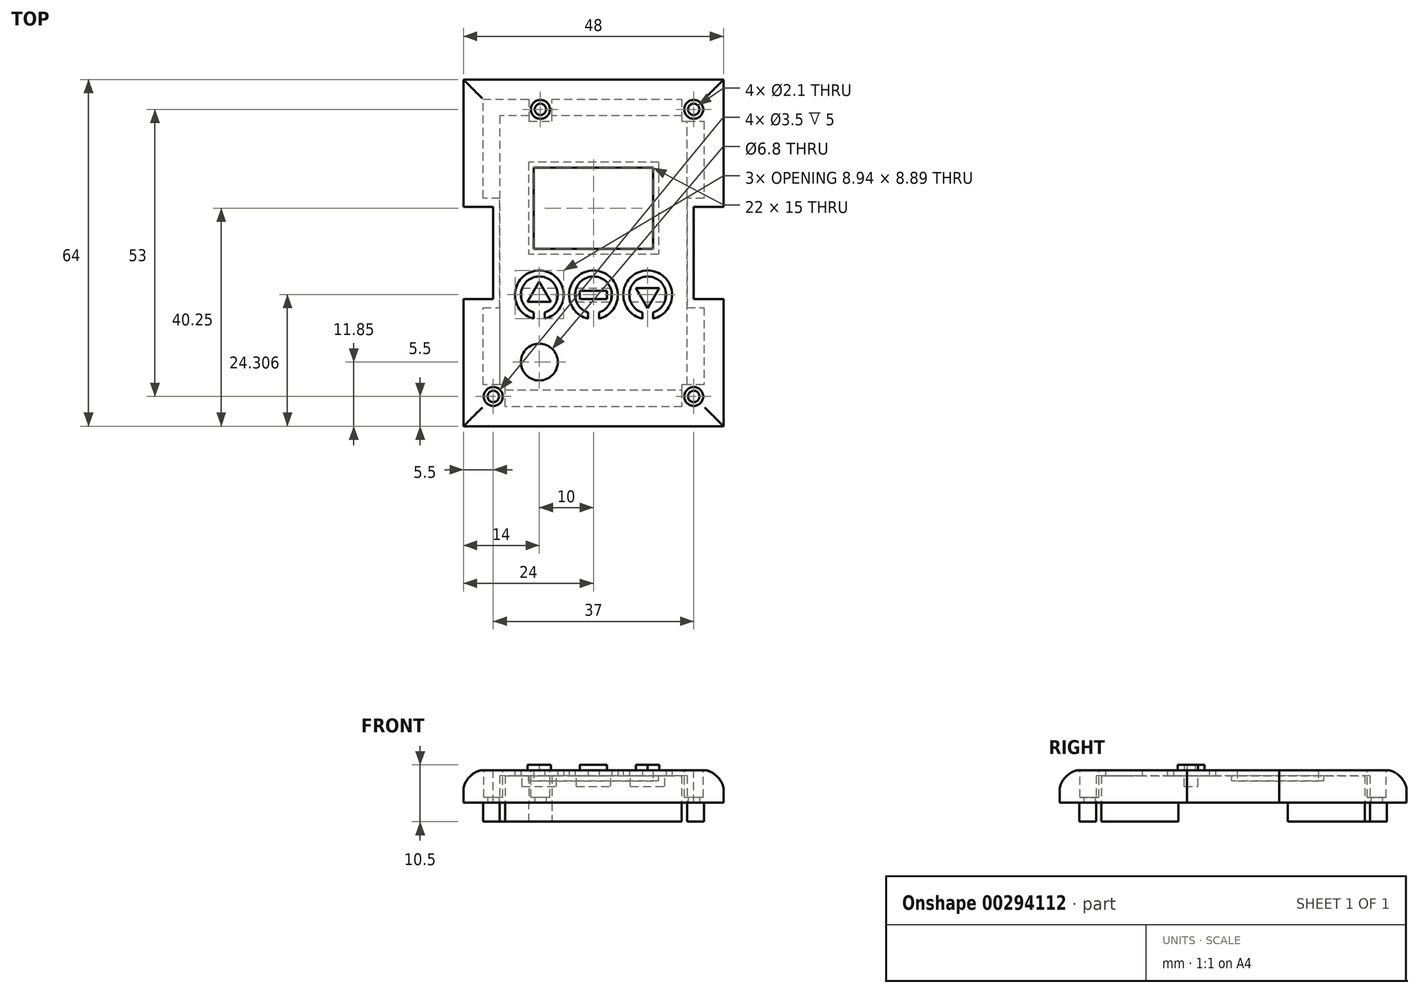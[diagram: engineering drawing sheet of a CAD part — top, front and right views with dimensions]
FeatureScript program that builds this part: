
annotation { "Feature Type Name" : "Feature", "Feature Type Description" : "" }
export const myFeature = defineFeature(function(context is Context, id is Id, definition is map)
    precondition{}
    {
        {
            var Q0;
            Q0=qCreatedBy(makeId("Top.planeOp"),FACE);
            var sketch = newSketch(context, id + "F0", { "sketchPlane" : qUnion([Q0])});
            skLineSegment(sketch, "E0.bottom", {"start": v(24, 32) * mm, "end": v(-24, 32) * mm});
            skLineSegment(sketch, "E0.top", {"start": v(24, -32) * mm, "end": v(-24, -32) * mm});
            skLineSegment(sketch, "E0.left", {"start": v(24, 32) * mm, "end": v(24, -32) * mm});
            skLineSegment(sketch, "E0.right", {"start": v(-24, 32) * mm, "end": v(-24, -32) * mm});
            skPoint(sketch, "E0.middle", {"position": v(0, 0) * mm});
            skSolve(sketch);
        }
        {
            var Q0;
            Q0=qSketchRegion(id+"F0",true);
            extrude(context, id + "F1", {"entities" : qUnion([Q0]), "depth" : 6 * mm});
        }
        {
            var Q0;
            Q0=makeQuery(id+"F1.opExtrude","CAP_FACE",FACE,{"disambiguationData":[OSD([sQuery(id+"F0.wireOp",EDGE,"E0.bottom"),sQuery(id+"F0.wireOp",EDGE,"E0.top"),sQuery(id+"F0.wireOp",EDGE,"E0.left"),sQuery(id+"F0.wireOp",EDGE,"E0.right")])],"isStart":false});
            var sketch = newSketch(context, id + "F2", { "sketchPlane" : qUnion([Q0])});
            skLineSegment(sketch, "E1.bottom", {"start": v(-24, 8.5) * mm, "end": v(-18.5, 8.5) * mm});
            skLineSegment(sketch, "E1.top", {"start": v(-24, -8.5) * mm, "end": v(-18.5, -8.5) * mm});
            skLineSegment(sketch, "E1.left", {"start": v(-24, 8.5) * mm, "end": v(-24, -8.5) * mm});
            skLineSegment(sketch, "E1.right", {"start": v(-18.5, 8.5) * mm, "end": v(-18.5, -8.5) * mm});
            skPoint(sketch, "E1.middle", {"position": v(-21.25, 0) * mm});
            skLineSegment(sketch, "E2.bottom", {"start": v(24, 8.5) * mm, "end": v(18.5, 8.5) * mm});
            skLineSegment(sketch, "E2.top", {"start": v(24, -8.5) * mm, "end": v(18.5, -8.5) * mm});
            skLineSegment(sketch, "E2.left", {"start": v(24, 8.5) * mm, "end": v(24, -8.5) * mm});
            skLineSegment(sketch, "E2.right", {"start": v(18.5, 8.5) * mm, "end": v(18.5, -8.5) * mm});
            skPoint(sketch, "E2.middle", {"position": v(21.25, 0) * mm});
            skSolve(sketch);
        }
        {
            var Q0;
            Q0=qSketchRegion(id+"F2",true);
            extrude(context, id + "F3", {"entities" : qUnion([Q0]), "operationType" : NewBodyOperationType.REMOVE, "endBound" : BoundingType.THROUGH_ALL, "oppositeDirection" : true, "depth" : 25 * mm});
        }
        {
            var Q0;
            Q0=makeQuery(id+"F1.opExtrude","CAP_FACE",FACE,{"disambiguationData":[OSD([sQuery(id+"F0.wireOp",EDGE,"E0.bottom"),sQuery(id+"F0.wireOp",EDGE,"E0.top"),sQuery(id+"F0.wireOp",EDGE,"E0.left"),sQuery(id+"F0.wireOp",EDGE,"E0.right")])],"isStart":true});
            var sketch = newSketch(context, id + "F4", { "sketchPlane" : qUnion([Q0])});
            skLineSegment(sketch, "E3", {"start": v(-20.4, -28.4) * mm, "end": v(-11.9, -28.4) * mm});
            skLineSegment(sketch, "E4", {"start": v(-11.9, -28.4) * mm, "end": v(-11.9, -24.3) * mm});
            skLineSegment(sketch, "E5", {"start": v(-11.9, -24.3) * mm, "end": v(-7.7, -24.3) * mm});
            skLineSegment(sketch, "E6", {"start": v(-7.7, -24.3) * mm, "end": v(-7.7, -28.4) * mm});
            skLineSegment(sketch, "E7", {"start": v(-7.7, -28.4) * mm, "end": v(16.3, -28.4) * mm});
            skLineSegment(sketch, "E8", {"start": v(16.3, -28.4) * mm, "end": v(16.3, -24.3) * mm});
            skLineSegment(sketch, "E9", {"start": v(16.3, -24.3) * mm, "end": v(20.4, -24.3) * mm});
            skLineSegment(sketch, "E10", {"start": v(20.4, -24.3) * mm, "end": v(20.4, -10.1) * mm});
            skLineSegment(sketch, "E11", {"start": v(20.4, -10.1) * mm, "end": v(15.5, -10.1) * mm});
            skLineSegment(sketch, "E12", {"start": v(15.5, -10.1) * mm, "end": v(15.5, 10.1) * mm});
            skLineSegment(sketch, "E13", {"start": v(15.5, 10.1) * mm, "end": v(20.4, 10.1) * mm});
            skLineSegment(sketch, "E14", {"start": v(20.4, 10.1) * mm, "end": v(20.4, 24.3) * mm});
            skLineSegment(sketch, "E15", {"start": v(20.4, 24.3) * mm, "end": v(16.3, 24.3) * mm});
            skLineSegment(sketch, "E16", {"start": v(16.3, 24.3) * mm, "end": v(16.3, 28.4) * mm});
            skLineSegment(sketch, "E17", {"start": v(16.3, 28.4) * mm, "end": v(-16.3, 28.4) * mm});
            skLineSegment(sketch, "E18", {"start": v(-16.3, 28.4) * mm, "end": v(-16.3, 24.3) * mm});
            skLineSegment(sketch, "E19", {"start": v(-16.3, 24.3) * mm, "end": v(-20.4, 24.3) * mm});
            skLineSegment(sketch, "E20", {"start": v(-20.4, 24.3) * mm, "end": v(-20.4, 10.1) * mm});
            skLineSegment(sketch, "E21", {"start": v(-20.4, 10.1) * mm, "end": v(-15.5, 10.1) * mm});
            skLineSegment(sketch, "E22", {"start": v(-15.5, 10.1) * mm, "end": v(-15.5, -10.1) * mm});
            skLineSegment(sketch, "E23", {"start": v(-15.5, -10.1) * mm, "end": v(-20.4, -10.1) * mm});
            skLineSegment(sketch, "E24", {"start": v(-20.4, -10.1) * mm, "end": v(-20.4, -28.4) * mm});
            skSolve(sketch);
        }
        {
            var Q0;
            Q0=qSketchRegion(id+"F4",true);
            extrude(context, id + "F5", {"entities" : qUnion([Q0]), "operationType" : NewBodyOperationType.ADD, "depth" : 3.5 * mm});
        }
        {
            var Q0;
            Q0=makeQuery(id+"F5.opExtrude","CAP_FACE",FACE,{"disambiguationData":[OSD([sQuery(id+"F4.wireOp",EDGE,"E3"),sQuery(id+"F4.wireOp",EDGE,"E4"),sQuery(id+"F4.wireOp",EDGE,"E5"),sQuery(id+"F4.wireOp",EDGE,"E6"),sQuery(id+"F4.wireOp",EDGE,"E7"),sQuery(id+"F4.wireOp",EDGE,"E8"),sQuery(id+"F4.wireOp",EDGE,"E9"),sQuery(id+"F4.wireOp",EDGE,"E10"),sQuery(id+"F4.wireOp",EDGE,"E11"),sQuery(id+"F4.wireOp",EDGE,"E12"),sQuery(id+"F4.wireOp",EDGE,"E13"),sQuery(id+"F4.wireOp",EDGE,"E14"),sQuery(id+"F4.wireOp",EDGE,"E15"),sQuery(id+"F4.wireOp",EDGE,"E16"),sQuery(id+"F4.wireOp",EDGE,"E17"),sQuery(id+"F4.wireOp",EDGE,"E18"),sQuery(id+"F4.wireOp",EDGE,"E19"),sQuery(id+"F4.wireOp",EDGE,"E20"),sQuery(id+"F4.wireOp",EDGE,"E21"),sQuery(id+"F4.wireOp",EDGE,"E22"),sQuery(id+"F4.wireOp",EDGE,"E23"),sQuery(id+"F4.wireOp",EDGE,"E24")])],"isStart":false});
            var sketch = newSketch(context, id + "F6", { "sketchPlane" : qUnion([Q0])});
            skLineSegment(sketch, "E25", {"start": v(-16.3, 24.3) * mm, "end": v(-16.3, 25.3) * mm});
            skLineSegment(sketch, "E26", {"start": v(-16.3, 25.3) * mm, "end": v(16.3, 25.3) * mm});
            skLineSegment(sketch, "E27", {"start": v(16.3, 25.3) * mm, "end": v(16.3, 24.3) * mm});
            skLineSegment(sketch, "E28", {"start": v(16.3, 24.3) * mm, "end": v(17.3, 24.3) * mm});
            skPoint(sketch, "E29.endSnap0", {"position": v(17.95, 10.1) * mm});
            skLineSegment(sketch, "E30", {"start": v(17.3, 24.3) * mm, "end": v(17.3, -24.3) * mm});
            skLineSegment(sketch, "E31", {"start": v(17.3, -24.3) * mm, "end": v(16.3, -24.3) * mm});
            skLineSegment(sketch, "E32", {"start": v(16.3, -24.3) * mm, "end": v(16.3, -25.3) * mm});
            skLineSegment(sketch, "E33", {"start": v(16.3, -25.3) * mm, "end": v(-7.7, -25.3) * mm});
            skLineSegment(sketch, "E34", {"start": v(-7.7, -25.3) * mm, "end": v(-7.7, -24.3) * mm});
            skLineSegment(sketch, "E35", {"start": v(-7.7, -24.3) * mm, "end": v(-11.9, -24.3) * mm});
            skLineSegment(sketch, "E36", {"start": v(-11.9, -24.3) * mm, "end": v(-11.9, -25.3) * mm});
            skLineSegment(sketch, "E37", {"start": v(-11.9, -25.3) * mm, "end": v(-17.3, -25.3) * mm});
            skLineSegment(sketch, "E38", {"start": v(-17.3, -25.3) * mm, "end": v(-17.3, 24.3) * mm});
            skLineSegment(sketch, "E39", {"start": v(-17.3, 24.3) * mm, "end": v(-16.3, 24.3) * mm});
            skSolve(sketch);
        }
        {
            var Q0;
            Q0=qSketchRegion(id+"F6",true);
            extrude(context, id + "F7", {"entities" : qUnion([Q0]), "operationType" : NewBodyOperationType.REMOVE, "oppositeDirection" : true, "depth" : 8.5 * mm});
        }
        {
            var Q0;
            Q0=makeQuery(id+"F1.opExtrude","CAP_FACE",FACE,{"disambiguationData":[OSD([sQuery(id+"F0.wireOp",EDGE,"E0.bottom"),sQuery(id+"F0.wireOp",EDGE,"E0.top"),sQuery(id+"F0.wireOp",EDGE,"E0.left"),sQuery(id+"F0.wireOp",EDGE,"E0.right")])],"isStart":true});
            var sketch = newSketch(context, id + "F8", { "sketchPlane" : qUnion([Q0])});
            skCircle(sketch, "E40", {"center": v(-18.5, 26.5) * mm, "radius": 1.05 * mm});
            skCircle(sketch, "E41", {"center": v(18.5, 26.5) * mm, "radius": 1.05 * mm});
            skCircle(sketch, "E42", {"center": v(18.5, -26.5) * mm, "radius": 1.05 * mm});
            skCircle(sketch, "E43", {"center": v(-9.8, -26.5) * mm, "radius": 1.05 * mm});
            skPoint(sketch, "E43.centerSnap0", {"position": v(-9.8, -24.3) * mm});
            skSolve(sketch);
        }
        {
            var Q0;
            Q0=qSketchRegion(id+"F8",true);
            extrude(context, id + "F9", {"entities" : qUnion([Q0]), "operationType" : NewBodyOperationType.REMOVE, "endBound" : BoundingType.THROUGH_ALL, "oppositeDirection" : true, "depth" : 25 * mm});
        }
        {
            var Q0;
            Q0=makeQuery(id+"F1.opExtrude","CAP_FACE",FACE,{"disambiguationData":[OSD([sQuery(id+"F0.wireOp",EDGE,"E0.bottom"),sQuery(id+"F0.wireOp",EDGE,"E0.top"),sQuery(id+"F0.wireOp",EDGE,"E0.left"),sQuery(id+"F0.wireOp",EDGE,"E0.right")])],"isStart":false});
            var sketch = newSketch(context, id + "F10", { "sketchPlane" : qUnion([Q0])});
            skCircle(sketch, "E44", {"center": v(-9.8, 26.5) * mm, "radius": 1.75 * mm});
            skCircle(sketch, "E45", {"center": v(18.5, 26.5) * mm, "radius": 1.75 * mm});
            skCircle(sketch, "E46", {"center": v(18.5, -26.5) * mm, "radius": 1.75 * mm});
            skCircle(sketch, "E47", {"center": v(-18.5, -26.5) * mm, "radius": 1.75 * mm});
            skSolve(sketch);
        }
        {
            var Q0;
            Q0=qSketchRegion(id+"F10",true);
            extrude(context, id + "F11", {"entities" : qUnion([Q0]), "operationType" : NewBodyOperationType.REMOVE, "oppositeDirection" : true, "depth" : 5 * mm});
        }
        {
            var Q0;
            Q0=makeQuery(id+"F7.boolean.opBoolean","COPY",FACE,{"derivedFrom":makeQuery(id+"F7.opExtrude","CAP_FACE",FACE,{"disambiguationData":[OSD([sQuery(id+"F6.wireOp",EDGE,"E25"),sQuery(id+"F6.wireOp",EDGE,"E26"),sQuery(id+"F6.wireOp",EDGE,"E27"),sQuery(id+"F6.wireOp",EDGE,"E28"),sQuery(id+"F6.wireOp",EDGE,"E30"),sQuery(id+"F6.wireOp",EDGE,"E31"),sQuery(id+"F6.wireOp",EDGE,"E32"),sQuery(id+"F6.wireOp",EDGE,"E33"),sQuery(id+"F6.wireOp",EDGE,"E34"),sQuery(id+"F6.wireOp",EDGE,"E35"),sQuery(id+"F6.wireOp",EDGE,"E36"),sQuery(id+"F6.wireOp",EDGE,"E37"),sQuery(id+"F6.wireOp",EDGE,"E38"),sQuery(id+"F6.wireOp",EDGE,"E39")])],"isStart":false})});
            var sketch = newSketch(context, id + "F12", { "sketchPlane" : qUnion([Q0])});
            skLineSegment(sketch, "E48.bottom", {"start": v(11, -0.75) * mm, "end": v(-11, -0.75) * mm});
            skLineSegment(sketch, "E48.top", {"start": v(11, -15.75) * mm, "end": v(-11, -15.75) * mm});
            skLineSegment(sketch, "E48.left", {"start": v(11, -0.75) * mm, "end": v(11, -15.75) * mm});
            skLineSegment(sketch, "E48.right", {"start": v(-11, -0.75) * mm, "end": v(-11, -15.75) * mm});
            skPoint(sketch, "E48.middle", {"position": v(0, -8.25) * mm});
            skSolve(sketch);
        }
        {
            var Q0;
            Q0=qSketchRegion(id+"F12",true);
            extrude(context, id + "F13", {"entities" : qUnion([Q0]), "operationType" : NewBodyOperationType.REMOVE, "endBound" : BoundingType.THROUGH_ALL, "oppositeDirection" : true, "depth" : 25 * mm});
        }
        {
            var Q0;
            Q0=makeQuery(id+"F7.boolean.opBoolean","COPY",FACE,{"derivedFrom":makeQuery(id+"F7.opExtrude","CAP_FACE",FACE,{"disambiguationData":[OSD([sQuery(id+"F6.wireOp",EDGE,"E25"),sQuery(id+"F6.wireOp",EDGE,"E26"),sQuery(id+"F6.wireOp",EDGE,"E27"),sQuery(id+"F6.wireOp",EDGE,"E28"),sQuery(id+"F6.wireOp",EDGE,"E30"),sQuery(id+"F6.wireOp",EDGE,"E31"),sQuery(id+"F6.wireOp",EDGE,"E32"),sQuery(id+"F6.wireOp",EDGE,"E33"),sQuery(id+"F6.wireOp",EDGE,"E34"),sQuery(id+"F6.wireOp",EDGE,"E35"),sQuery(id+"F6.wireOp",EDGE,"E36"),sQuery(id+"F6.wireOp",EDGE,"E37"),sQuery(id+"F6.wireOp",EDGE,"E38"),sQuery(id+"F6.wireOp",EDGE,"E39")])],"isStart":false})});
            var sketch = newSketch(context, id + "F14", { "sketchPlane" : qUnion([Q0])});
            skArc(sketch, "E49", {"start": v(-1, 11) * mm, "mid": v(0, 4.35) * mm, "end": v(1, 11) * mm});
            skArc(sketch, "E50", {"start": v(-1, 12.14) * mm, "mid": v(0, 3.25) * mm, "end": v(1, 12.14) * mm});
            skLineSegment(sketch, "E51", {"start": v(-1, 12.14) * mm, "end": v(-1, 11) * mm});
            skLineSegment(sketch, "E52", {"start": v(1, 12.14) * mm, "end": v(1, 11) * mm});
            skArc(sketch, "E53", {"start": v(11, 11) * mm, "mid": v(10, 4.35) * mm, "end": v(9, 11) * mm});
            skArc(sketch, "E54", {"start": v(11, 12.14) * mm, "mid": v(10, 3.25) * mm, "end": v(9, 12.14) * mm});
            skLineSegment(sketch, "E55", {"start": v(11, 11) * mm, "end": v(11, 12.14) * mm});
            skLineSegment(sketch, "E56", {"start": v(9, 11) * mm, "end": v(9, 12.14) * mm});
            skArc(sketch, "E57", {"start": v(-9, 11) * mm, "mid": v(-10, 4.35) * mm, "end": v(-11, 11) * mm});
            skArc(sketch, "E58", {"start": v(-9, 12.14) * mm, "mid": v(-10, 3.25) * mm, "end": v(-11, 12.14) * mm});
            skLineSegment(sketch, "E59", {"start": v(-9, 11) * mm, "end": v(-9, 12.14) * mm});
            skLineSegment(sketch, "E60", {"start": v(-11, 12.14) * mm, "end": v(-11, 11) * mm});
            skSolve(sketch);
        }
        {
            var Q0;
            Q0=qSketchRegion(id+"F14",true);
            extrude(context, id + "F15", {"entities" : qUnion([Q0]), "operationType" : NewBodyOperationType.REMOVE, "endBound" : BoundingType.THROUGH_ALL, "oppositeDirection" : true, "depth" : 25 * mm});
        }
        {
            var Q0;
            Q0=makeQuery(id+"F7.boolean.opBoolean","COPY",FACE,{"derivedFrom":makeQuery(id+"F7.opExtrude","CAP_FACE",FACE,{"disambiguationData":[OSD([sQuery(id+"F6.wireOp",EDGE,"E25"),sQuery(id+"F6.wireOp",EDGE,"E26"),sQuery(id+"F6.wireOp",EDGE,"E27"),sQuery(id+"F6.wireOp",EDGE,"E28"),sQuery(id+"F6.wireOp",EDGE,"E30"),sQuery(id+"F6.wireOp",EDGE,"E31"),sQuery(id+"F6.wireOp",EDGE,"E32"),sQuery(id+"F6.wireOp",EDGE,"E33"),sQuery(id+"F6.wireOp",EDGE,"E34"),sQuery(id+"F6.wireOp",EDGE,"E35"),sQuery(id+"F6.wireOp",EDGE,"E36"),sQuery(id+"F6.wireOp",EDGE,"E37"),sQuery(id+"F6.wireOp",EDGE,"E38"),sQuery(id+"F6.wireOp",EDGE,"E39")])],"isStart":false})});
            var sketch = newSketch(context, id + "F16", { "sketchPlane" : qUnion([Q0])});
            skLineSegment(sketch, "E61.bottom", {"start": v(-13.16, 9) * mm, "end": v(-6.84, 9) * mm});
            skLineSegment(sketch, "E61.top", {"start": v(-13.16, 6.5) * mm, "end": v(-6.84, 6.5) * mm});
            skLineSegment(sketch, "E61.left", {"start": v(-13.16, 9) * mm, "end": v(-13.16, 6.5) * mm});
            skLineSegment(sketch, "E61.right", {"start": v(-6.84, 9) * mm, "end": v(-6.84, 6.5) * mm});
            skLineSegment(sketch, "E62.bottom", {"start": v(-3.16, 9) * mm, "end": v(3.16, 9) * mm});
            skLineSegment(sketch, "E62.top", {"start": v(-3.16, 6.5) * mm, "end": v(3.16, 6.5) * mm});
            skLineSegment(sketch, "E62.left", {"start": v(-3.16, 9) * mm, "end": v(-3.16, 6.5) * mm});
            skLineSegment(sketch, "E62.right", {"start": v(3.16, 9) * mm, "end": v(3.16, 6.5) * mm});
            skLineSegment(sketch, "E63.bottom", {"start": v(6.84, 9) * mm, "end": v(13.16, 9) * mm});
            skLineSegment(sketch, "E63.top", {"start": v(6.84, 6.5) * mm, "end": v(13.16, 6.5) * mm});
            skLineSegment(sketch, "E63.left", {"start": v(6.84, 9) * mm, "end": v(6.84, 6.5) * mm});
            skLineSegment(sketch, "E63.right", {"start": v(13.16, 9) * mm, "end": v(13.16, 6.5) * mm});
            skSolve(sketch);
        }
        {
            var Q0;
            Q0=qSketchRegion(id+"F16",true);
            extrude(context, id + "F17", {"entities" : qUnion([Q0]), "operationType" : NewBodyOperationType.ADD, "depth" : 2 * mm});
        }
        {
            var Q0;
            Q0=makeQuery(id+"F1.opExtrude","CAP_FACE",FACE,{"disambiguationData":[OSD([sQuery(id+"F0.wireOp",EDGE,"E0.bottom"),sQuery(id+"F0.wireOp",EDGE,"E0.top"),sQuery(id+"F0.wireOp",EDGE,"E0.left"),sQuery(id+"F0.wireOp",EDGE,"E0.right")])],"isStart":false});
            var sketch = newSketch(context, id + "F18", { "sketchPlane" : qUnion([Q0])});
            skCircle(sketch, "E64.cCircle", {"center": v(10, -7.75) * mm, "radius": 2.5 * mm, "construction": true});
            skLineSegment(sketch, "E64.0", {"start": v(10, -10.25) * mm, "end": v(7.83, -6.5) * mm});
            skLineSegment(sketch, "E64.1", {"start": v(7.83, -6.5) * mm, "end": v(12.17, -6.5) * mm});
            skLineSegment(sketch, "E64.2", {"start": v(12.17, -6.5) * mm, "end": v(10, -10.25) * mm});
            skCircle(sketch, "E65.cCircle", {"center": v(-10, -7.75) * mm, "radius": 2.5 * mm, "construction": true});
            skLineSegment(sketch, "E65.0", {"start": v(-12.17, -9) * mm, "end": v(-10, -5.25) * mm});
            skLineSegment(sketch, "E65.1", {"start": v(-10, -5.25) * mm, "end": v(-7.83, -9) * mm});
            skLineSegment(sketch, "E65.2", {"start": v(-7.83, -9) * mm, "end": v(-12.17, -9) * mm});
            skLineSegment(sketch, "E66.bottom", {"start": v(-2.5, -8.5) * mm, "end": v(2.5, -8.5) * mm});
            skLineSegment(sketch, "E66.top", {"start": v(-2.5, -7) * mm, "end": v(2.5, -7) * mm});
            skLineSegment(sketch, "E66.left", {"start": v(-2.5, -8.5) * mm, "end": v(-2.5, -7) * mm});
            skLineSegment(sketch, "E66.right", {"start": v(2.5, -8.5) * mm, "end": v(2.5, -7) * mm});
            skPoint(sketch, "E66.middle", {"position": v(0, -7.75) * mm});
            skSolve(sketch);
        }
        {
            var Q0;
            Q0=qSketchRegion(id+"F18",true);
            extrude(context, id + "F19", {"entities" : qUnion([Q0]), "operationType" : NewBodyOperationType.ADD, "depth" : 1 * mm});
        }
        {
            var Q0;
            Q0=makeQuery(id+"F7.boolean.opBoolean","COPY",FACE,{"derivedFrom":makeQuery(id+"F7.opExtrude","CAP_FACE",FACE,{"disambiguationData":[OSD([sQuery(id+"F6.wireOp",EDGE,"E25"),sQuery(id+"F6.wireOp",EDGE,"E26"),sQuery(id+"F6.wireOp",EDGE,"E27"),sQuery(id+"F6.wireOp",EDGE,"E28"),sQuery(id+"F6.wireOp",EDGE,"E30"),sQuery(id+"F6.wireOp",EDGE,"E31"),sQuery(id+"F6.wireOp",EDGE,"E32"),sQuery(id+"F6.wireOp",EDGE,"E33"),sQuery(id+"F6.wireOp",EDGE,"E34"),sQuery(id+"F6.wireOp",EDGE,"E35"),sQuery(id+"F6.wireOp",EDGE,"E36"),sQuery(id+"F6.wireOp",EDGE,"E37"),sQuery(id+"F6.wireOp",EDGE,"E38"),sQuery(id+"F6.wireOp",EDGE,"E39")])],"isStart":false})});
            var sketch = newSketch(context, id + "F20", { "sketchPlane" : qUnion([Q0])});
            skLineSegment(sketch, "E67.bottom", {"start": v(-11, -0.75) * mm, "end": v(11, -0.75) * mm});
            skLineSegment(sketch, "E67.top", {"start": v(-11, -15.75) * mm, "end": v(11, -15.75) * mm});
            skLineSegment(sketch, "E67.left", {"start": v(-11, -0.75) * mm, "end": v(-11, -15.75) * mm});
            skLineSegment(sketch, "E67.right", {"start": v(11, -0.75) * mm, "end": v(11, -15.75) * mm});
            skLineSegment(sketch, "E68.bottom", {"start": v(12, -16.75) * mm, "end": v(-12, -16.75) * mm});
            skLineSegment(sketch, "E68.top", {"start": v(12, 0.25) * mm, "end": v(-12, 0.25) * mm});
            skLineSegment(sketch, "E68.left", {"start": v(12, -16.75) * mm, "end": v(12, 0.25) * mm});
            skLineSegment(sketch, "E68.right", {"start": v(-12, -16.75) * mm, "end": v(-12, 0.25) * mm});
            skSolve(sketch);
        }
        {
            var Q0;
            Q0=qSketchRegion(id+"F20",true);
            extrude(context, id + "F21", {"entities" : qUnion([Q0]), "operationType" : NewBodyOperationType.ADD, "depth" : 1 * mm});
        }
        {
            var Q0;
            {var subQ0=sQuery(id+"F0.wireOp",EDGE,"E0.bottom");var subQ1=sQuery(id+"F0.wireOp",EDGE,"E0.left");Q0=makeQuery(id+"F3.boolean.opBoolean","SPLIT",EDGE,{"disambiguationData":[TD([makeQuery(id+"F1.opExtrude","SWEPT_FACE",FACE,{"disambiguationData":[OSD([subQ0])]})])],"derivedFrom":makeQuery(id+"F1.opExtrude","CAP_EDGE",EDGE,{"disambiguationData":[OSD([subQ1])],"isStart":false})});}
            var Q1;
            Q1=makeQuery(id+"F1.opExtrude","CAP_EDGE",EDGE,{"disambiguationData":[OSD([sQuery(id+"F0.wireOp",EDGE,"E0.bottom")])],"isStart":false});
            var Q2;
            {var subQ0=sQuery(id+"F0.wireOp",EDGE,"E0.bottom");var subQ1=sQuery(id+"F0.wireOp",EDGE,"E0.right");Q2=makeQuery(id+"F3.boolean.opBoolean","SPLIT",EDGE,{"disambiguationData":[TD([makeQuery(id+"F1.opExtrude","SWEPT_FACE",FACE,{"disambiguationData":[OSD([subQ0])]})])],"derivedFrom":makeQuery(id+"F1.opExtrude","CAP_EDGE",EDGE,{"disambiguationData":[OSD([subQ1])],"isStart":false})});}
            var Q3;
            {var subQ0=sQuery(id+"F0.wireOp",EDGE,"E0.right");var subQ1=sQuery(id+"F0.wireOp",EDGE,"E0.top");Q3=makeQuery(id+"F3.boolean.opBoolean","SPLIT",EDGE,{"disambiguationData":[TD([makeQuery(id+"F1.opExtrude","SWEPT_FACE",FACE,{"disambiguationData":[OSD([subQ1])]})])],"derivedFrom":makeQuery(id+"F1.opExtrude","CAP_EDGE",EDGE,{"disambiguationData":[OSD([subQ0])],"isStart":false})});}
            var Q4;
            Q4=makeQuery(id+"F1.opExtrude","CAP_EDGE",EDGE,{"disambiguationData":[OSD([sQuery(id+"F0.wireOp",EDGE,"E0.top")])],"isStart":false});
            var Q5;
            {var subQ0=sQuery(id+"F0.wireOp",EDGE,"E0.left");var subQ1=sQuery(id+"F0.wireOp",EDGE,"E0.top");Q5=makeQuery(id+"F3.boolean.opBoolean","SPLIT",EDGE,{"disambiguationData":[TD([makeQuery(id+"F1.opExtrude","SWEPT_FACE",FACE,{"disambiguationData":[OSD([subQ1])]})])],"derivedFrom":makeQuery(id+"F1.opExtrude","CAP_EDGE",EDGE,{"disambiguationData":[OSD([subQ0])],"isStart":false})});}
            fillet(context, id + "F22", {"entities" : qUnion([Q0, Q1, Q2, Q3, Q4, Q5]), "radius" : 3.5 * mm, "tangentPropagation" : true, "rho" : 0.33, "crossSection" : FilletCrossSection.CONIC, "allowEdgeOverflow" : false});
        }
        {
            var Q0;
            Q0=makeQuery(id+"F7.boolean.opBoolean","COPY",FACE,{"derivedFrom":makeQuery(id+"F7.opExtrude","CAP_FACE",FACE,{"disambiguationData":[OSD([sQuery(id+"F6.wireOp",EDGE,"E25"),sQuery(id+"F6.wireOp",EDGE,"E26"),sQuery(id+"F6.wireOp",EDGE,"E27"),sQuery(id+"F6.wireOp",EDGE,"E28"),sQuery(id+"F6.wireOp",EDGE,"E30"),sQuery(id+"F6.wireOp",EDGE,"E31"),sQuery(id+"F6.wireOp",EDGE,"E32"),sQuery(id+"F6.wireOp",EDGE,"E33"),sQuery(id+"F6.wireOp",EDGE,"E34"),sQuery(id+"F6.wireOp",EDGE,"E35"),sQuery(id+"F6.wireOp",EDGE,"E36"),sQuery(id+"F6.wireOp",EDGE,"E37"),sQuery(id+"F6.wireOp",EDGE,"E38"),sQuery(id+"F6.wireOp",EDGE,"E39")])],"isStart":false})});
            var sketch = newSketch(context, id + "F23", { "sketchPlane" : qUnion([Q0])});
            skCircle(sketch, "E69", {"center": v(-10, 20.15) * mm, "radius": 3.4 * mm});
            skSolve(sketch);
        }
        {
            var Q0;
            Q0=qSketchRegion(id+"F23",true);
            extrude(context, id + "F24", {"entities" : qUnion([Q0]), "operationType" : NewBodyOperationType.REMOVE, "endBound" : BoundingType.THROUGH_ALL, "oppositeDirection" : true, "depth" : 25 * mm});
        }
    });
